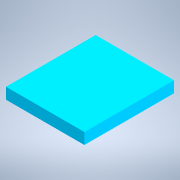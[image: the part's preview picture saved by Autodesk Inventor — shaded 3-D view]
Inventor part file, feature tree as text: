
AUTODESK INVENTOR PART (.ipt)
format: ipt  version: 2022.3 (Build 263350000, 350)  size: 100,864 bytes
history: native  units: in
note: dims shown in document units (in); Inventor stores cm internally (conversion verified against a paired STEP export)
features: extrude x1, sketch x1
ambient origin geometry x8: Origin, YZ Plane, XZ Plane, XY Plane, X Axis, Y Axis, Z Axis, Center Point
bodies: Solid1 (feature_tree)
feature tree (2):
  extrude  "Extrusion1"  Depth=0.7in
  sketch  "Sketch1"  dims[d0=0.8in d1=0.7in d2=0.1in d3=0.0in]
